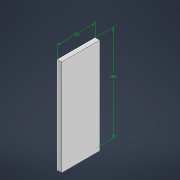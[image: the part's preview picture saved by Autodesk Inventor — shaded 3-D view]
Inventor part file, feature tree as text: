
AUTODESK INVENTOR PART (.ipt)
format: ipt  version: 2022 (Build 260153000, 153)  size: 88,064 bytes
history: native  units: mm
features: extrude x1, sketch x1
ambient origin geometry x8: Origin, YZ Plane, XZ Plane, XY Plane, X Axis, Y Axis, Z Axis, Center Point
bodies: Body1 (feature_tree)
feature tree (2):
  extrude  "Выдавливание2"  Depth=105.0mm
  sketch  "Эскиз2"
